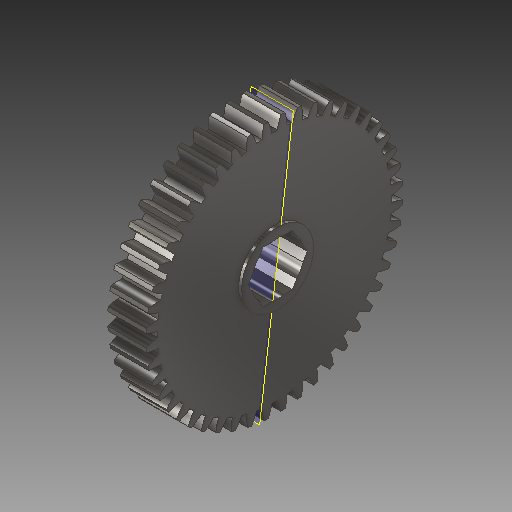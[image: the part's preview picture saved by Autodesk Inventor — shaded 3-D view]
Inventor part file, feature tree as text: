
AUTODESK INVENTOR PART (.ipt)
format: ipt  version: 2018 (Build 220112000, 112)  size: 462,336 bytes
history: native  units: in
note: dims shown in document units (in); Inventor stores cm internally (conversion verified against a paired STEP export)
features: plane x1, other x1
ambient origin geometry x8: Origin, YZ Plane, XZ Plane, XY Plane, X Axis, Y Axis, Z Axis, Center Point
bodies: Solid1 (feature_tree)
feature tree (2):
  plane  "Work Plane2"
  other  "Bore"
